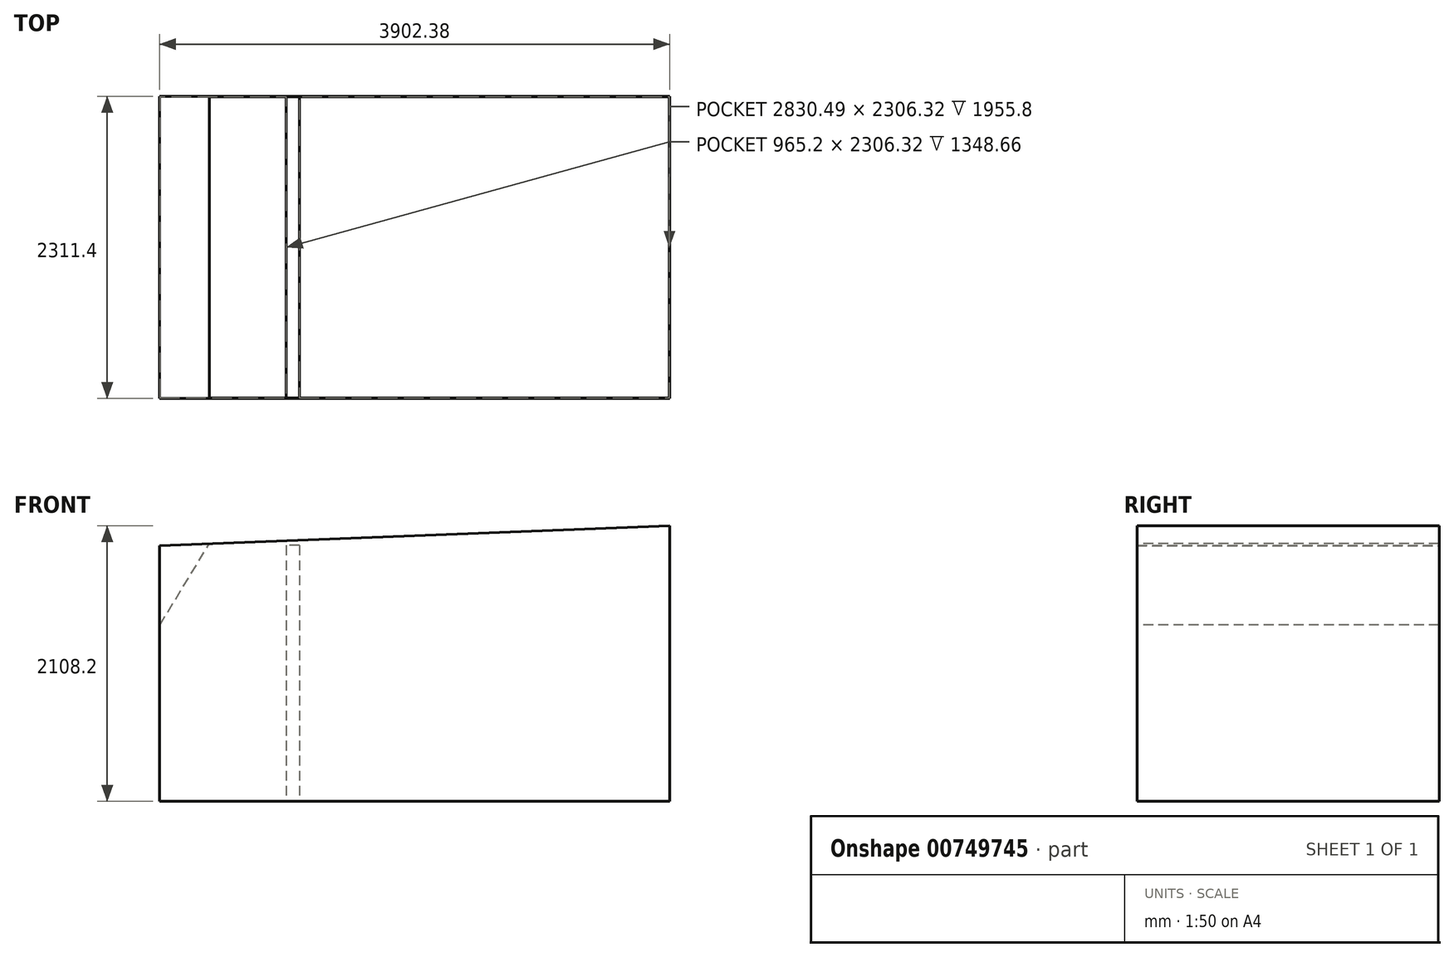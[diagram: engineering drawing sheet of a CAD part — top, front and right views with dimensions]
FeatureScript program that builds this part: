
annotation { "Feature Type Name" : "Feature", "Feature Type Description" : "" }
export const myFeature = defineFeature(function(context is Context, id is Id, definition is map)
    precondition{}
    {
        {
            var Q0;
            Q0=qCreatedBy(makeId("Front.planeOp"),FACE);
            var sketch = newSketch(context, id + "F0", { "sketchPlane" : qUnion([Q0])});
            skLineSegment(sketch, "E0", {"start": v(-1948.07, 877.6) * mm, "end": v(1954.3, 1030) * mm});
            skLineSegment(sketch, "E1", {"start": v(1954.3, 1030) * mm, "end": v(1954.3, -1078.2) * mm});
            skLineSegment(sketch, "E2", {"start": v(1954.3, -1078.2) * mm, "end": v(-1948.07, -1078.2) * mm});
            skLineSegment(sketch, "E3", {"start": v(-1948.07, -1078.2) * mm, "end": v(-1948.07, 877.6) * mm});
            skSolve(sketch);
        }
        {
            var Q0;
            Q0=qSketchRegion(id+"F0",true);
            extrude(context, id + "F1", {"entities" : qUnion([Q0]), "depth" : 2311.4 * mm, "offsetDistance" : 25.4 * mm});
        }
        {
            var Q0;
            Q0=makeQuery(id+"F1.opExtrude","SWEPT_FACE",FACE,{"disambiguationData":[OSD([sQuery(id+"F0.wireOp",EDGE,"E0")])]});
            shell(context, id + "F2", {"entities" : qUnion([Q0]), "thickness" : 2.54 * mm});
        }
        {
            var Q0;
            Q0=makeQuery(id+"F2.opShell","OFFSET_FACE",FACE,{"disambiguationData":[OSD([sQuery(id+"F0.wireOp",EDGE,"E2")])]});
            var sketch = newSketch(context, id + "F3", { "sketchPlane" : qUnion([Q0])});
            skLineSegment(sketch, "E4.0", {"start": v(-878.73, -2308.86) * mm, "end": v(-878.73, -2.54) * mm});
            skLineSegment(sketch, "E5.0", {"start": v(-980.33, -2308.86) * mm, "end": v(-980.33, -2.54) * mm});
            skLineSegment(sketch, "E6", {"start": v(-980.33, -2.54) * mm, "end": v(-878.73, -2.54) * mm});
            skLineSegment(sketch, "E7", {"start": v(-980.33, -2308.86) * mm, "end": v(-878.73, -2308.86) * mm});
            skSolve(sketch);
        }
        {
            var Q0;
            Q0=qSketchRegion(id+"F3",true);
            extrude(context, id + "F4", {"entities" : qUnion([Q0]), "operationType" : NewBodyOperationType.ADD, "depth" : 1955.8 * mm, "offsetDistance" : 25.4 * mm});
        }
        {
            var Q0;
            Q0=makeQuery(id+"F1.opExtrude","CAP_FACE",FACE,{"disambiguationData":[OSD([sQuery(id+"F0.wireOp",EDGE,"E0"),sQuery(id+"F0.wireOp",EDGE,"E1"),sQuery(id+"F0.wireOp",EDGE,"E2"),sQuery(id+"F0.wireOp",EDGE,"E3")])],"isStart":false});
            var sketch = newSketch(context, id + "F5", { "sketchPlane" : qUnion([Q0])});
            skLineSegment(sketch, "E8", {"start": v(-1948.07, 268.83) * mm, "end": v(-1567.9, 892.45) * mm});
            skLineSegment(sketch, "E9", {"start": v(-1567.9, 892.45) * mm, "end": v(-1948.07, 877.6) * mm});
            skLineSegment(sketch, "E10", {"start": v(-1948.07, 877.6) * mm, "end": v(-1948.07, 268.83) * mm});
            skSolve(sketch);
        }
        {
            var Q0;
            Q0=qSketchRegion(id+"F5",true);
            extrude(context, id + "F6", {"entities" : qUnion([Q0]), "operationType" : NewBodyOperationType.ADD, "oppositeDirection" : true, "depth" : 2311.4 * mm, "offsetDistance" : 25.4 * mm});
        }
    });
